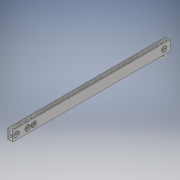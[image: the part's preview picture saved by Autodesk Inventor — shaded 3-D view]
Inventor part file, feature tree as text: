
AUTODESK INVENTOR PART (.ipt)
format: ipt  version: 2018 (Build 220112000, 112)  size: 150,016 bytes
history: native  units: in
note: dims shown in document units (in); Inventor stores cm internally (conversion verified against a paired STEP export)
features: sketch x5, extrude x5, plane x1
ambient origin geometry x8: Origin, YZ Plane, XZ Plane, XY Plane, X Axis, Y Axis, Z Axis, Center Point
bodies: Body1 (feature_tree)
feature tree (11):
  sketch  "Sketch1"  dims[d0=1.0in d1=32.0in]
  plane  "Work Plane3"
  extrude  "Extrusion3"  Depth=32.0in
  extrude  "Extrusion5"  Depth=0.125in TaperAngle=0.0deg
  extrude  "Extrusion6"  Depth=0.125in
  extrude  "Extrusion10"  Depth=0.125in TaperAngle=0.0deg
  extrude  "Extrusion11"  Depth=1.0in
  sketch  "Sketch2"  dims[d2=0.125in d7=0.125in d8=0.0in]
  sketch  "Sketch4"  dims[d11=2.0in d12=0.0in d13=0.125in]
  sketch  "Sketch5"  dims[d14=0.125in d15=40.0in d16=0.0in]
  sketch  "Sketch6"  dims[d17=0.75in d18=1.0in d19=1.125in d22=2.25in d23=1.125in d26=1.25in d27=1.125in d30=2.0in d31=0.0in d32=1.25in d33=1.125in d34=3.0in d35=0.0in]
